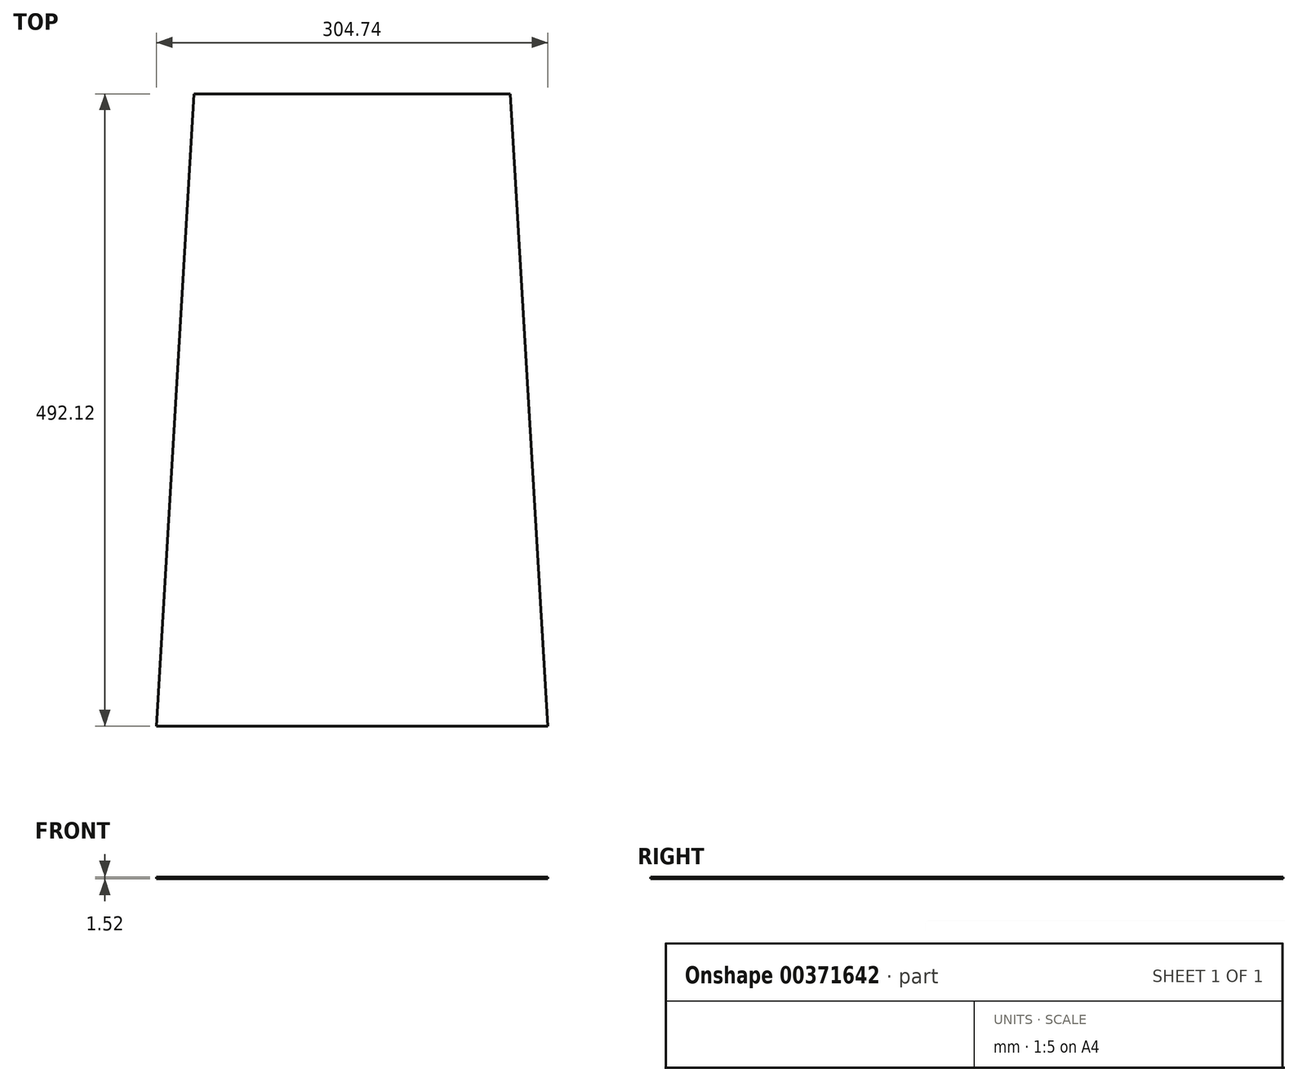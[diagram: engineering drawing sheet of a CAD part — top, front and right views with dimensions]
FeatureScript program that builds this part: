
annotation { "Feature Type Name" : "Feature", "Feature Type Description" : "" }
export const myFeature = defineFeature(function(context is Context, id is Id, definition is map)
    precondition{}
    {
        {
            var Q0;
            Q0=qCreatedBy(makeId("Top.planeOp"),FACE);
            var sketch = newSketch(context, id + "F0", { "sketchPlane" : qUnion([Q0])});
            skLineSegment(sketch, "E0", {"start": v(0, 0) * mm, "end": v(342.9, 0) * mm});
            skLineSegment(sketch, "E1", {"start": v(342.9, 0) * mm, "end": v(342.9, 533.4) * mm, "construction": true});
            skLineSegment(sketch, "E2", {"start": v(342.9, 533.4) * mm, "end": v(311.15, 533.4) * mm, "construction": true});
            skLineSegment(sketch, "E3", {"start": v(0, 533.4) * mm, "end": v(0, 0) * mm, "construction": true});
            skLineSegment(sketch, "E4", {"start": v(0, 0) * mm, "end": v(31.75, 533.4) * mm});
            skLineSegment(sketch, "E5", {"start": v(31.75, 533.4) * mm, "end": v(0, 533.4) * mm, "construction": true});
            skLineSegment(sketch, "E6", {"start": v(0, 533.4) * mm, "end": v(0, 533.4) * mm});
            skLineSegment(sketch, "E7", {"start": v(311.15, 533.4) * mm, "end": v(342.9, 0) * mm});
            skLineSegment(sketch, "E8", {"start": v(311.15, 533.4) * mm, "end": v(31.75, 533.4) * mm});
            skLineSegment(sketch, "E9", {"start": v(342.9, 533.4) * mm, "end": v(342.9, 533.4) * mm});
            skSolve(sketch);
        }
        {
            var Q0;
            Q0=makeQuery(id+"F0.imprint","IMPRINT",FACE,{"disambiguationData":[TD([[makeQuery(id+"F0.imprint","IMPRINT",EDGE,{"derivedFrom":sQuery(id+"F0.wireOp",EDGE,"E0")}),1.0]])]});
            extrude(context, id + "F1", {"entities" : qUnion([Q0]), "depth" : 1.52 * mm});
        }
        {
            var Q0;
            Q0=makeQuery(id+"F1.opExtrude","CAP_FACE",FACE,{"disambiguationData":[OSD([sQuery(id+"F0.wireOp",EDGE,"E0"),sQuery(id+"F0.wireOp",EDGE,"E4"),sQuery(id+"F0.wireOp",EDGE,"E7"),sQuery(id+"F0.wireOp",EDGE,"E8")])],"isStart":false});
            var sketch = newSketch(context, id + "F2", { "sketchPlane" : qUnion([Q0])});
            skLineSegment(sketch, "E10", {"start": v(19.08, 0) * mm, "end": v(48.38, 492.13) * mm});
            skLineSegment(sketch, "E11", {"start": v(48.38, 492.13) * mm, "end": v(294.52, 492.13) * mm});
            skLineSegment(sketch, "E12", {"start": v(294.52, 492.13) * mm, "end": v(323.82, 0) * mm});
            skLineSegment(sketch, "E13", {"start": v(19.08, 0) * mm, "end": v(-8.59, -41.4) * mm});
            skLineSegment(sketch, "E14", {"start": v(-8.59, -41.4) * mm, "end": v(-8.59, 593.9) * mm});
            skLineSegment(sketch, "E15", {"start": v(-8.59, 593.9) * mm, "end": v(381.2, 593.9) * mm});
            skLineSegment(sketch, "E16", {"start": v(381.2, 593.9) * mm, "end": v(381.2, -41.4) * mm});
            skLineSegment(sketch, "E17", {"start": v(381.2, -41.4) * mm, "end": v(323.82, 0) * mm});
            skSolve(sketch);
        }
        {
            var Q0;
            {var subQ4=sQuery(id+"F2.wireOp",EDGE,"E10");Q0=makeQuery(id+"F2.imprint","IMPRINT",FACE,{"disambiguationData":[TD([[makeQuery(id+"F2.imprint","IMPRINT",EDGE,{"derivedFrom":subQ4}),1.0]])]});}
            extrude(context, id + "F3", {"entities" : qUnion([Q0]), "operationType" : NewBodyOperationType.REMOVE, "endBound" : BoundingType.THROUGH_ALL, "oppositeDirection" : true, "depth" : 25.4 * mm});
        }
    });
